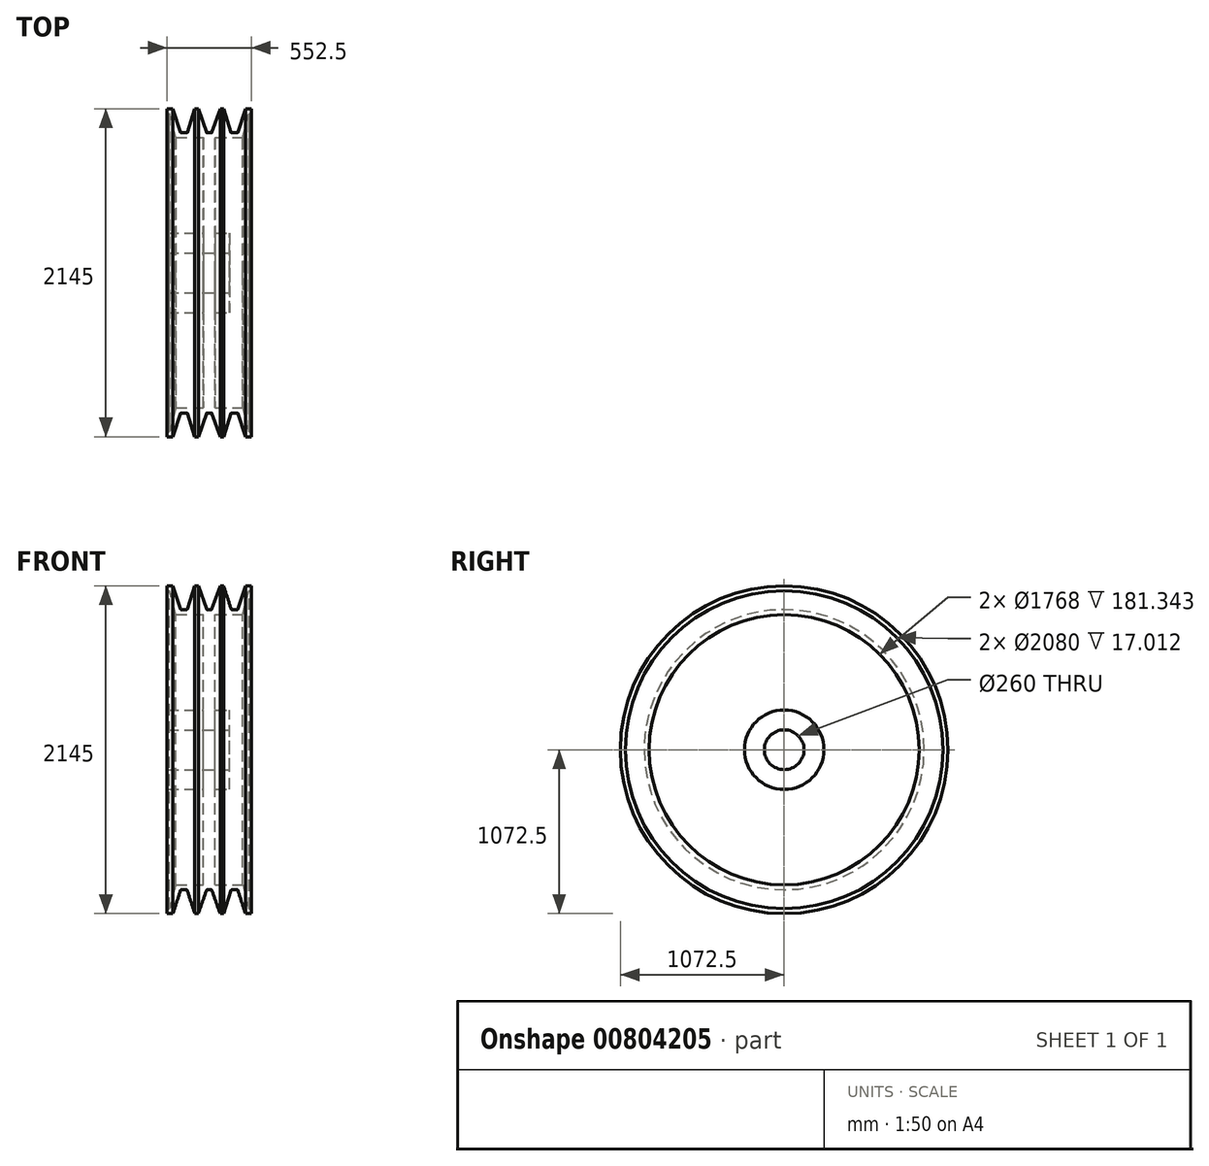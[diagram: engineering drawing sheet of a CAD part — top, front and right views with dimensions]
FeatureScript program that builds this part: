
annotation { "Feature Type Name" : "Feature", "Feature Type Description" : "" }
export const myFeature = defineFeature(function(context is Context, id is Id, definition is map)
    precondition{}
    {
        {
            var Q0;
            Q0=qCreatedBy(makeId("Front.planeOp"),FACE);
            var sketch = newSketch(context, id + "F0", { "sketchPlane" : qUnion([Q0])});
            skLineSegment(sketch, "E0", {"start": v(0, 0) * mm, "end": v(0, 1650) * mm, "construction": true});
            skLineSegment(sketch, "E1", {"start": v(0, 1650) * mm, "end": v(425, 1650) * mm, "construction": true});
            skLineSegment(sketch, "E2", {"start": v(425, 1650) * mm, "end": v(425, 1360) * mm, "construction": true});
            skLineSegment(sketch, "E3", {"start": v(425, 1650) * mm, "end": v(314.55, 1650) * mm});
            skLineSegment(sketch, "E4", {"start": v(255, 1360) * mm, "end": v(255, 1650) * mm, "construction": true});
            skLineSegment(sketch, "E5", {"start": v(425, 1650) * mm, "end": v(365, 1650) * mm});
            skLineSegment(sketch, "E6", {"start": v(365, 1650) * mm, "end": v(287.02, 1410) * mm});
            skLineSegment(sketch, "E7", {"start": v(425, 1600) * mm, "end": v(398.83, 1600) * mm});
            skLineSegment(sketch, "E8", {"start": v(398.83, 1600) * mm, "end": v(338.99, 1360) * mm});
            skLineSegment(sketch, "E9.MirrorCS", {"start": v(145, 1650) * mm, "end": v(222.98, 1410) * mm});
            skLineSegment(sketch, "E10", {"start": v(145, 1650) * mm, "end": v(110, 1650) * mm});
            skLineSegment(sketch, "E11", {"start": v(110, 1650) * mm, "end": v(25.4, 1410) * mm});
            skLineSegment(sketch, "E12", {"start": v(222.98, 1410) * mm, "end": v(287.02, 1410) * mm});
            skLineSegment(sketch, "E13", {"start": v(25.4, 1410) * mm, "end": v(0, 1410) * mm});
            skLineSegment(sketch, "E14", {"start": v(255, 1360) * mm, "end": v(338.99, 1360) * mm});
            skLineSegment(sketch, "E15", {"start": v(255, 1360) * mm, "end": v(0, 1360) * mm});
            skLineSegment(sketch, "E16", {"start": v(338.99, 1360) * mm, "end": v(425, 1360) * mm, "construction": true});
            skLineSegment(sketch, "E17", {"start": v(0, 1410) * mm, "end": v(25.4, 1410) * mm});
            skLineSegment(sketch, "E18.MirrorCS", {"start": v(-25.4, 1410) * mm, "end": v(0, 1410) * mm});
            skLineSegment(sketch, "E19.MirrorCS", {"start": v(-110, 1650) * mm, "end": v(-25.4, 1410) * mm});
            skLineSegment(sketch, "E20.MirrorCS", {"start": v(-145, 1650) * mm, "end": v(-110, 1650) * mm});
            skLineSegment(sketch, "E21.MirrorCS", {"start": v(-145, 1650) * mm, "end": v(-222.98, 1410) * mm});
            skLineSegment(sketch, "E22.MirrorCS", {"start": v(-222.98, 1410) * mm, "end": v(-287.02, 1410) * mm});
            skLineSegment(sketch, "E23.MirrorCS", {"start": v(-365, 1650) * mm, "end": v(-287.02, 1410) * mm});
            skLineSegment(sketch, "E24.MirrorCS", {"start": v(-425, 1650) * mm, "end": v(-365, 1650) * mm});
            skLineSegment(sketch, "E25.MirrorCS", {"start": v(-425, 1600) * mm, "end": v(-398.83, 1600) * mm});
            skLineSegment(sketch, "E26.MirrorCS", {"start": v(-398.83, 1600) * mm, "end": v(-338.99, 1360) * mm});
            skLineSegment(sketch, "E27.MirrorCS", {"start": v(-255, 1360) * mm, "end": v(-338.99, 1360) * mm});
            skLineSegment(sketch, "E28.MirrorCS", {"start": v(0, 2720) * mm, "end": v(0, 1070) * mm, "construction": true});
            skLineSegment(sketch, "E29.MirrorCS", {"start": v(-255, 1360) * mm, "end": v(0, 1360) * mm});
            skLineSegment(sketch, "E30", {"start": v(-425, 1600) * mm, "end": v(-425, 1650) * mm});
            skLineSegment(sketch, "E31", {"start": v(0, 0) * mm, "end": v(-425, 0) * mm});
            skLineSegment(sketch, "E32", {"start": v(-425, 0) * mm, "end": v(-425, 400) * mm});
            skLineSegment(sketch, "E33", {"start": v(-425, 400) * mm, "end": v(225, 400) * mm});
            skLineSegment(sketch, "E34", {"start": v(225, 0) * mm, "end": v(0, 0) * mm});
            skLineSegment(sketch, "E35", {"start": v(225, 400) * mm, "end": v(225, 0) * mm});
            skLineSegment(sketch, "E36", {"start": v(-425, 200) * mm, "end": v(225, 200) * mm});
            skLineSegment(sketch, "E37", {"start": v(60, 400) * mm, "end": v(60, 1360) * mm});
            skLineSegment(sketch, "E38.MirrorCS", {"start": v(-60, 400) * mm, "end": v(-60, 1360) * mm});
            skLineSegment(sketch, "E39", {"start": v(425, 1650) * mm, "end": v(425, 1600) * mm});
            skSolve(sketch);
        }
        {
            var Q0;
            {var subQ7=sQuery(id+"F0.wireOp",EDGE,"E36");Q0=makeQuery(id+"F0.imprint","IMPRINT",FACE,{"disambiguationData":[TD([[makeQuery(id+"F0.imprint","IMPRINT",EDGE,{"derivedFrom":subQ7}),1.0]])]});}
            var Q1;
            {var subQ0=sQuery(id+"F0.wireOp",EDGE,"E37");Q1=makeQuery(id+"F0.imprint","IMPRINT",FACE,{"disambiguationData":[TD([[makeQuery(id+"F0.imprint","IMPRINT",EDGE,{"derivedFrom":subQ0}),1.0]])]});}
            var Q2;
            {var subQ6=sQuery(id+"F0.wireOp",EDGE,"E6");Q2=makeQuery(id+"F0.imprint","IMPRINT",FACE,{"disambiguationData":[TD([[makeQuery(id+"F0.imprint","IMPRINT",EDGE,{"derivedFrom":subQ6}),1.0]])]});}
            var Q3;
            Q3=sQuery(id+"F0.wireOp",EDGE,"E34");
            revolve(context, id + "F1", {"surfaceOperationType" : NewSurfaceOperationType.NEW, "entities" : qUnion([Q0, Q1, Q2]), "axis" : qUnion([Q3]), "revolveType" : RevolveType.FULL});
        }
        {
            var Q0;
            Q0=makeQuery(id+"F1.opRevolve","SWEPT_EDGE",EDGE,{"disambiguationData":[OSD([sQuery(id+"F0.wireOp",EDGE,"E6"),sQuery(id+"F0.wireOp",EDGE,"E12")])]});
            var Q1;
            Q1=makeQuery(id+"F1.opRevolve","SWEPT_EDGE",EDGE,{"disambiguationData":[OSD([sQuery(id+"F0.wireOp",EDGE,"E9.MirrorCS"),sQuery(id+"F0.wireOp",EDGE,"E12")])]});
            var Q2;
            Q2=makeQuery(id+"F1.opRevolve","SWEPT_EDGE",EDGE,{"disambiguationData":[OSD([sQuery(id+"F0.wireOp",EDGE,"E11"),sQuery(id+"F0.wireOp",EDGE,"E13")])]});
            var Q3;
            Q3=makeQuery(id+"F1.opRevolve","SWEPT_EDGE",EDGE,{"disambiguationData":[OSD([sQuery(id+"F0.wireOp",EDGE,"E18.MirrorCS"),sQuery(id+"F0.wireOp",EDGE,"E19.MirrorCS")])]});
            var Q4;
            Q4=makeQuery(id+"F1.opRevolve","SWEPT_EDGE",EDGE,{"disambiguationData":[OSD([sQuery(id+"F0.wireOp",EDGE,"E21.MirrorCS"),sQuery(id+"F0.wireOp",EDGE,"E22.MirrorCS")])]});
            var Q5;
            Q5=makeQuery(id+"F1.opRevolve","SWEPT_EDGE",EDGE,{"disambiguationData":[OSD([sQuery(id+"F0.wireOp",EDGE,"E22.MirrorCS"),sQuery(id+"F0.wireOp",EDGE,"E23.MirrorCS")])]});
            fillet(context, id + "F2", {"entities" : qUnion([Q0, Q1, Q2, Q3, Q4, Q5]), "radius" : 5 * mm, "tangentPropagation" : true, "allowEdgeOverflow" : false});
        }
        {
            var Q0;
            Q0=makeQuery(id+"F1.opRevolve","SWEPT_BODY",BODY,{"disambiguationData":[OSD([sQuery(id+"F0.wireOp",EDGE,"E3"),sQuery(id+"F0.wireOp",EDGE,"E6"),sQuery(id+"F0.wireOp",EDGE,"E7"),sQuery(id+"F0.wireOp",EDGE,"E8"),sQuery(id+"F0.wireOp",EDGE,"E9.MirrorCS"),sQuery(id+"F0.wireOp",EDGE,"E10"),sQuery(id+"F0.wireOp",EDGE,"E11"),sQuery(id+"F0.wireOp",EDGE,"E12"),sQuery(id+"F0.wireOp",EDGE,"E13"),sQuery(id+"F0.wireOp",EDGE,"E14"),sQuery(id+"F0.wireOp",EDGE,"E15"),sQuery(id+"F0.wireOp",EDGE,"E18.MirrorCS"),sQuery(id+"F0.wireOp",EDGE,"E19.MirrorCS"),sQuery(id+"F0.wireOp",EDGE,"E20.MirrorCS"),sQuery(id+"F0.wireOp",EDGE,"E21.MirrorCS"),sQuery(id+"F0.wireOp",EDGE,"E22.MirrorCS"),sQuery(id+"F0.wireOp",EDGE,"E23.MirrorCS"),sQuery(id+"F0.wireOp",EDGE,"E24.MirrorCS"),sQuery(id+"F0.wireOp",EDGE,"E25.MirrorCS"),sQuery(id+"F0.wireOp",EDGE,"E26.MirrorCS"),sQuery(id+"F0.wireOp",EDGE,"E27.MirrorCS"),sQuery(id+"F0.wireOp",EDGE,"E29.MirrorCS"),sQuery(id+"F0.wireOp",EDGE,"E30"),sQuery(id+"F0.wireOp",EDGE,"E32"),sQuery(id+"F0.wireOp",EDGE,"E33"),sQuery(id+"F0.wireOp",EDGE,"E35"),sQuery(id+"F0.wireOp",EDGE,"E36"),sQuery(id+"F0.wireOp",EDGE,"E37"),sQuery(id+"F0.wireOp",EDGE,"E38.MirrorCS"),sQuery(id+"F0.wireOp",EDGE,"E39")])]});
            var Q1;
            Q1=qCreatedBy(makeId("Origin.pointOp"),VERTEX);
            var Q2;
            Q2=qCreatedBy(makeId("Origin.pointOp"),VERTEX);
            transform(context, id + "F3", {"entities" : qUnion([Q0]), "transformType" : TransformType.SCALE_UNIFORMLY, "scale" : .65, "scalePoint" : qUnion([Q2]), "makeCopy" : false});
        }
        {
            var Q0;
            Q0=makeQuery(id+"F1.opRevolve","SWEPT_FACE",FACE,{"disambiguationData":[OSD([sQuery(id+"F0.wireOp",EDGE,"E37")])]});
            var sketch = newSketch(context, id + "F4", { "sketchPlane" : qUnion([Q0])});
            skCircle(sketch, "E40", {"center": v(0, 0) * mm, "radius": 4.45 * mm});
            skSolve(sketch);
        }
        {
            var Q0;
            Q0=makeQuery(id+"F4.imprint","IMPRINT",FACE,{"disambiguationData":[TD([[makeQuery(id+"F4.imprint","IMPRINT",EDGE,{"derivedFrom":sQuery(id+"F4.wireOp",EDGE,"E40")}),1.0]])]});
            var Q1;
            Q1=makeQuery(id+"F1.opRevolve","SWEPT_FACE",FACE,{"disambiguationData":[OSD([sQuery(id+"F0.wireOp",EDGE,"E35")])]});
            extrude(context, id + "F5", {"entities" : qUnion([Q0, Q1]), "operationType" : NewBodyOperationType.REMOVE, "endBound" : BoundingType.SYMMETRIC, "oppositeDirection" : true, "depth" : 25.4 * mm, "offsetDistance" : 25.4 * mm});
        }
    });
